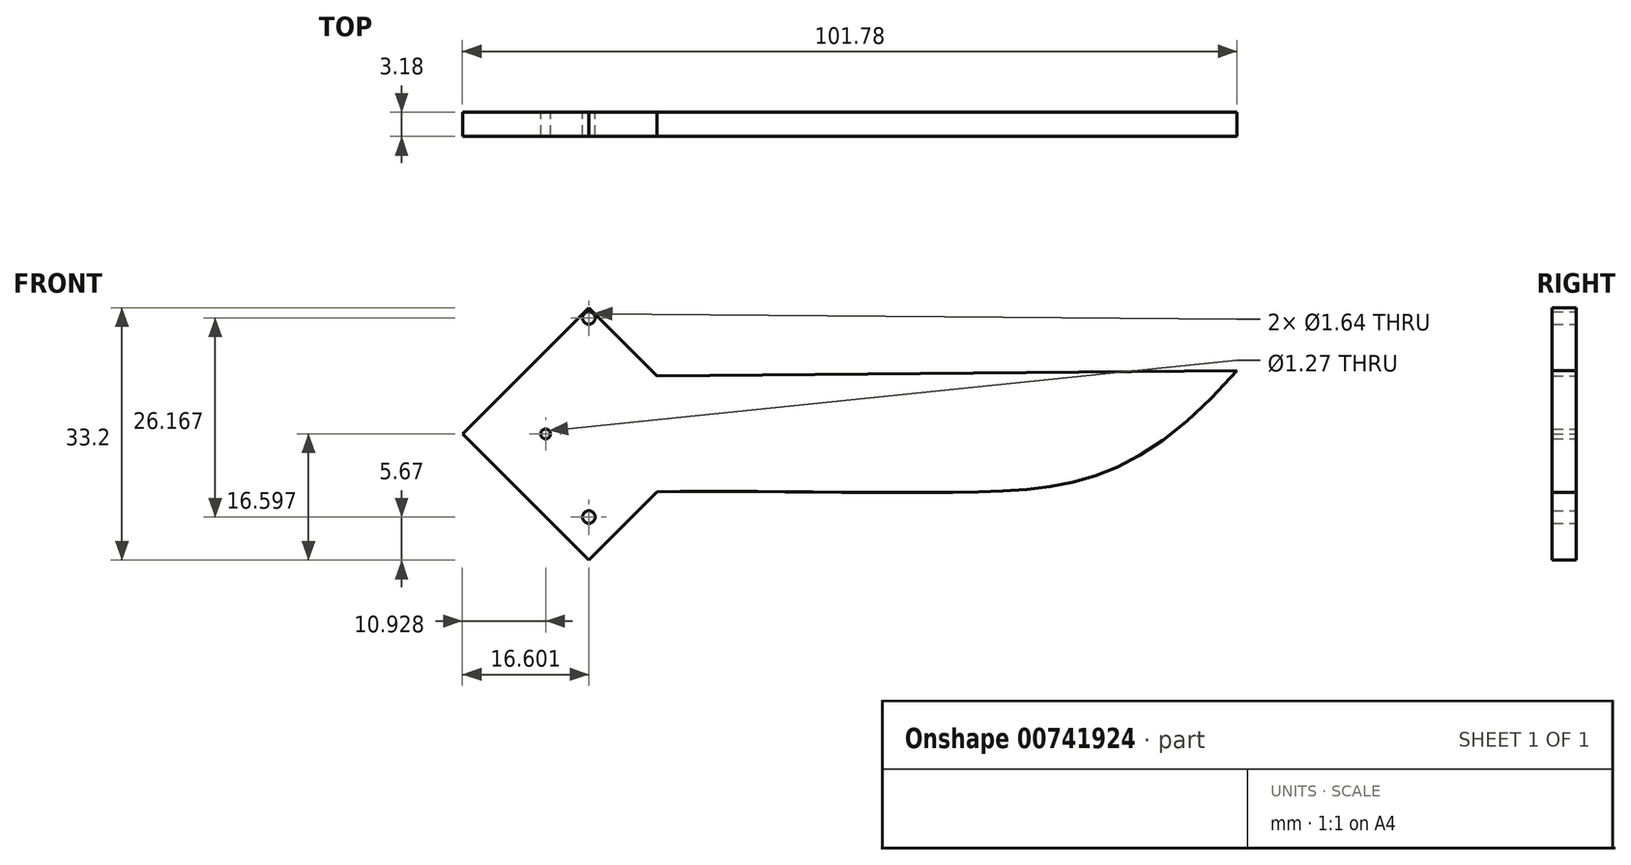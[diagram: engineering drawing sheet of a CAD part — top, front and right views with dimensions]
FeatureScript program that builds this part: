
annotation { "Feature Type Name" : "Feature", "Feature Type Description" : "" }
export const myFeature = defineFeature(function(context is Context, id is Id, definition is map)
    precondition{}
    {
        {
            var Q0;
            Q0=qCreatedBy(makeId("Front.planeOp"),FACE);
            var sketch = newSketch(context, id + "F0", { "sketchPlane" : qUnion([Q0])});
            skLineSegment(sketch, "E0", {"start": v(-48.47, 22.65) * mm, "end": v(-47.1, 24) * mm});
            skLineSegment(sketch, "E1", {"start": v(-47.1, 24) * mm, "end": v(-38.13, 15.03) * mm});
            skLineSegment(sketch, "E2", {"start": v(-52.78, -3.52) * mm, "end": v(-47.1, -9.2) * mm});
            skLineSegment(sketch, "E3", {"start": v(-47.1, -9.2) * mm, "end": v(-38.13, -0.21) * mm});
            skCircle(sketch, "E4", {"center": v(-47.1, 22.65) * mm, "radius": 0.82 * mm});
            skCircle(sketch, "E5", {"center": v(-47.1, -3.52) * mm, "radius": 0.82 * mm});
            skLineSegment(sketch, "E6", {"start": v(-48.47, 22.65) * mm, "end": v(-63.7, 7.4) * mm});
            skLineSegment(sketch, "E7", {"start": v(-52.78, -3.52) * mm, "end": v(-63.7, 7.4) * mm});
            skLineSegment(sketch, "E8", {"start": v(-38.13, 15.03) * mm, "end": v(38.07, 15.76) * mm});
            skFitSpline(sketch, "E9", {"points": [v(-38.13, -0.21) * mm, v(3.1, -0.21) * mm, v(38.07, 15.76) * mm], "startDerivative": vector(66.72, 1.26) * mm, "endDerivative": vector(80.25, 91.3) * mm});
            skCircle(sketch, "E10", {"center": v(-52.78, 7.4) * mm, "radius": 0.64 * mm});
            skSolve(sketch);
        }
        {
            var Q0;
            Q0=makeQuery(id+"F0.imprint","IMPRINT",FACE,{"disambiguationData":[TD([[makeQuery(id+"F0.imprint","IMPRINT",EDGE,{"derivedFrom":sQuery(id+"F0.wireOp",EDGE,"E0")}),-1.0]])]});
            extrude(context, id + "F1", {"entities" : qUnion([Q0]), "depth" : 3.17 * mm, "offsetDistance" : 25.4 * mm});
        }
    });
